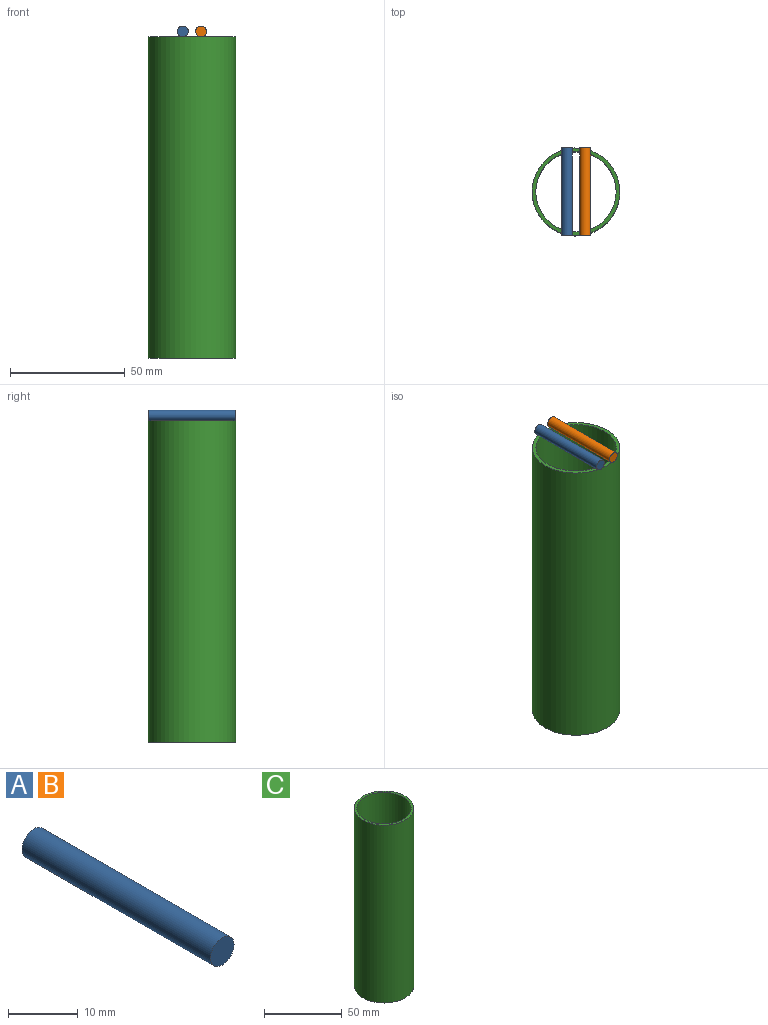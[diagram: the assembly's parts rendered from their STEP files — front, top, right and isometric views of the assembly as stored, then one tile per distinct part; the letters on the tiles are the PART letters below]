
ASSEMBLY  parts=3 mates=1
PART A: 3 faces, bbox 4.8x38.1x4.8 mm
  f0: cylinder r=2.38mm len=38.1mm, axis (0,-1,0), area 570mm2, adj f1,f2
  f1: plane 4.76x4.76mm, normal (0,1,0), area 17.8mm2, adj f0
  f2: plane 4.76x4.76mm, normal (0,-1,0), area 17.8mm2, adj f0
PART B: same geometry as A
PART C: 4 faces, bbox 38.1x38.1x139.7 mm
  f0: cylinder r=19.05mm len=139.7mm, axis (0,0,-1), area 16721.3mm2, adj f1,f2
  f1: plane 38.1x38.1mm, normal (0,0,1), area 182.1mm2, adj f0,f3
  f2: plane 38.1x38.1mm, normal (0,0,-1), area 182.1mm2, adj f0,f3
  f3: cylinder r=17.46mm len=139.7mm, axis (0,0,-1), area 15327.9mm2, adj f1,f2
PLACE A t=(-3.18,-57.15,78.58)mm
PLACE B rot(axis=(1,0,0),180deg) t=(4.76,-19.05,78.58)mm
PLACE C t=(0.79,-38.1,-63.5)mm
MATE fastened A.f0 <-> B.f1  axis (0,-1,0) through (-3.18,-57.15,78.58)mm
